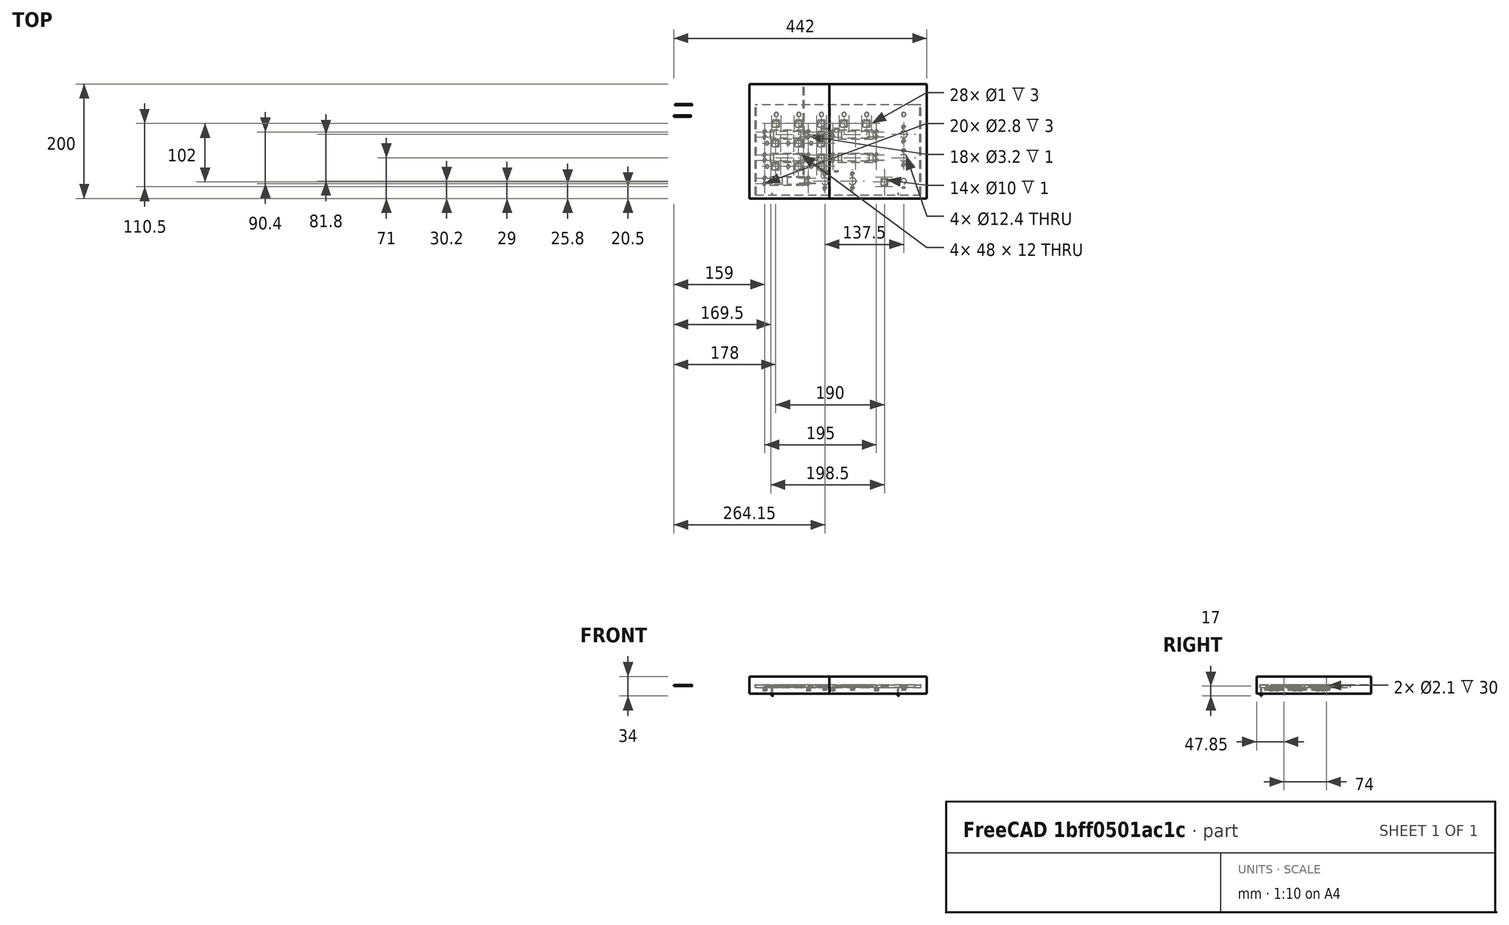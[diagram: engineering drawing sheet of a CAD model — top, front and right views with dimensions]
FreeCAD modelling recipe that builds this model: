
FCSTD DOCUMENT  (FreeCAD 0.17R13522 (Git))
Label: panel_frente_principal_con_spacers
License: CreativeCommons Attribution-ShareAlike
LicenseURL: http://creativecommons.org/licenses/by-sa/4.0/
objects: Part::Feature×53, Part::Cut×43, Part::Part2DObjectPython×22, Part::Fuse×22, Part::Box×13, Part::Cylinder×6, App::DocumentObjectGroup×3
note: 159 computed .brp shape members not serialized (recipe doc carries the construction recipe); baked Part::Feature solids carry a one-line shape summary decoded from their .brp

FEATURE [Part::Part2DObjectPython] Line009  # Draft 2D object (typed FeaturePython)
  ChamferSize = 0
  Closed = false
  End = (270.847,20.2,0)
  FilletRadius = 0
  Length = 35.3471
  MakeFace = false
  Points = (2) [(235.5,20.2,0),(270.847,20.2,0)]
  Start = (235.5,20.2,0)
  Subdivisions = 0
FEATURE [Part::Part2DObjectPython] Circle001  # Draft 2D object (typed FeaturePython)
  FirstAngle = 0
  LastAngle = 0
  MakeFace = false
  Placement = pos=(259.67,20.2,0) rot=(0,0,1;0rad)
  Radius = 14
FEATURE [Part::Part2DObjectPython] Line014  # Draft 2D object (typed FeaturePython)
  ChamferSize = 0
  Closed = false
  End = (248.272,28.2144,0)
  FilletRadius = 0
  Length = 13.696
  MakeFace = false
  Placement = pos=(-10,0,-4) rot=(0,0,1;0rad)
  Points = (2) [(269.378,20.2,4),(258.272,28.2144,4)]
  Start = (259.378,20.2,0)
  Subdivisions = 0
FEATURE [Part::Part2DObjectPython] Line015  # Draft 2D object (typed FeaturePython)
  ChamferSize = 0
  Closed = false
  End = (254.876,33.263,0)
  FilletRadius = 0
  Length = 13.7518
  MakeFace = false
  Placement = pos=(-10,0,-4) rot=(0,0,1;0rad)
  Points = (2) [(269.174,20.2,4),(264.876,33.263,4)]
  Start = (259.174,20.2,0)
  Subdivisions = 0
FEATURE [Part::Part2DObjectPython] Line016  # Draft 2D object (typed FeaturePython)
  ChamferSize = 0
  Closed = false
  End = (263.227,33.6931,0)
  FilletRadius = 0
  Length = 14.1488
  MakeFace = false
  Placement = pos=(-10,0,-4) rot=(0,0,1;0rad)
  Points = (2) [(268.97,20.2,4),(273.227,33.6931,4)]
  Start = (258.97,20.2,0)
  Subdivisions = 0
FEATURE [Part::Part2DObjectPython] Line017  # Draft 2D object (typed FeaturePython)
  ChamferSize = 0
  Closed = false
  End = (270.612,28.9289,0)
  FilletRadius = 0
  Length = 14.5511
  MakeFace = false
  Placement = pos=(-10,0,-4) rot=(0,0,1;0rad)
  Points = (2) [(268.97,20.2,4),(280.612,28.9289,4)]
  Start = (258.97,20.2,0)
  Subdivisions = 0
FEATURE [App::DocumentObjectGroup] Construction
  Group = -> [Line009,Circle001,Line014,Line015,Line016,Line017]
FEATURE [Part::Box] Box001  label="Cube"
  AttacherType = Attacher::AttachEngine3D
  Height = 3
  Length = 6
  Placement = pos=(39,81,-108) rot=(0,0,1;0rad)
  Width = 6
FEATURE [Part::Feature] Fusion008001001061001  label="panel_siplays_encoders_dobles_y_spacers"
  Placement = pos=(0,0,-105) rot=(0,0,1;0rad)
  shape: bbox 280 x 210 x 10 mm, 411 faces (baked)
FEATURE [Part::Feature] Fusion003002001  label="el perforador001"
  Placement = pos=(48,115,-108) rot=(0,1,0;3.14159rad)
  shape: bbox 22 x 12 x 18 mm, 19 faces (baked)
FEATURE [Part::Feature] Fusion003002001001  label="el perforador002"
  Placement = pos=(87.5,115,-108) rot=(0,1,0;3.14159rad)
  shape: bbox 22 x 12 x 18 mm, 19 faces (baked)
FEATURE [Part::Cut] Cut001001001002003001008002002004
  Base = -> Fusion008001001061001
  Refine = true
  Tool = -> Fusion003002001
FEATURE [Part::Feature] Fusion003002001001001  label="el perforador003"
  Placement = pos=(127,115,-108) rot=(0,1,0;3.14159rad)
  shape: bbox 22 x 12 x 18 mm, 19 faces (baked)
FEATURE [Part::Cut] Cut001001001002003001008002002005
  Base = -> Cut001001001002003001008002002004
  Refine = true
  Tool = -> Fusion003002001001
FEATURE [Part::Feature] Fusion003002001001001001  label="el perforador004"
  Placement = pos=(166.5,115,-108) rot=(0,1,0;3.14159rad)
  shape: bbox 22 x 12 x 18 mm, 19 faces (baked)
FEATURE [Part::Feature] Fusion003002001001001001001  label="el perforador005"
  Placement = pos=(206,115,-108) rot=(0,1,0;3.14159rad)
  shape: bbox 22 x 12 x 18 mm, 19 faces (baked)
FEATURE [Part::Cut] Cut001001001002003001008002002006
  Base = -> Cut001001001002003001008002002005
  Refine = true
  Tool = -> Fusion003002001001001001
FEATURE [Part::Cut] Cut001001001002003001008002002007
  Base = -> Cut001001001002003001008002002006
  Refine = true
  Tool = -> Fusion003002001001001001001
FEATURE [Part::Feature] Fusion003002001001001001002001001  label="el perforador008"
  Placement = pos=(127,40,-108) rot=(0,1,0;3.14159rad)
  shape: bbox 22 x 12 x 18 mm, 19 faces (baked)
FEATURE [Part::Feature] Fusion003002001001001001002001002  label="el perforador009"
  Placement = pos=(127,80.5,-108) rot=(0,1,0;3.14159rad)
  shape: bbox 22 x 12 x 18 mm, 19 faces (baked)
FEATURE [Part::Feature] Fusion003002001001001001002001  label="el perforador007"
  Placement = pos=(127,55,-108) rot=(0,1,0;3.14159rad)
  shape: bbox 22 x 12 x 18 mm, 19 faces (baked)
FEATURE [Part::Feature] Fusion003002001001001001002  label="el perforador006"
  Placement = pos=(127,95.5,-108) rot=(0,1,0;3.14159rad)
  shape: bbox 22 x 12 x 18 mm, 19 faces (baked)
FEATURE [Part::Cut] Cut001001001002003001008002002008
  Base = -> Cut001001001002003001008002002007
  Refine = true
  Tool = -> Fusion003002001001001
FEATURE [Part::Cut] Cut001001001002003001008002002009
  Base = -> Cut001001001002003001008002002008
  Refine = true
  Tool = -> Fusion003002001001001001002
FEATURE [Part::Cut] Cut001001001002003001008002002010
  Base = -> Cut001001001002003001008002002009
  Refine = true
  Tool = -> Fusion003002001001001001002001
FEATURE [Part::Box] Box001001002002002001003001001004001001001001001001002  label="Cube034"
  AttacherType = Attacher::AttachEngine3D
  Height = 4
  Length = 32
  Placement = pos=(200,15,-108) rot=(0,0,1;0rad)
  Width = 10
FEATURE [Part::Fuse] Fusion003002001001001001002001003
  Base = -> Cut001001001002003001008002002010
  Refine = true
  Tool = -> Box001001002002002001003001001004001001001001001001002
FEATURE [Part::Fuse] Fusion003002001001001001002001004
  Base = -> Box001001002002002001003001001004001001001001001001002
  Refine = true
  Tool = -> Fusion003002001001001001002001003
FEATURE [Part::Fuse] Fusion003002001001001001002001005
  Refine = true
  Tool = -> Fusion003002001001001001002001004
FEATURE [Part::Fuse] Fusion003002001001001001002001006
  Base = -> Box001
  Refine = true
  Tool = -> Fusion003002001001001001002001005
FEATURE [Part::Feature] Fusion003002001001001001002001002001  label="el perforador010"
  Placement = pos=(47,80.5,-108) rot=(0,1,0;3.14159rad)
  shape: bbox 22 x 12 x 18 mm, 19 faces (baked)
FEATURE [Part::Feature] Fusion003002001001001001002001002002  label="el perforador011"
  Placement = pos=(87,80.5,-108) rot=(0,1,0;3.14159rad)
  shape: bbox 22 x 12 x 18 mm, 19 faces (baked)
FEATURE [Part::Feature] Fusion003002001001001001002001001001  label="el perforador012"
  Placement = pos=(87,40,-108) rot=(0,1,0;3.14159rad)
  shape: bbox 22 x 12 x 18 mm, 19 faces (baked)
FEATURE [Part::Feature] Fusion003002001001001001002001001001001  label="el perforador013"
  Placement = pos=(47,40,-108) rot=(0,1,0;3.14159rad)
  shape: bbox 22 x 12 x 18 mm, 19 faces (baked)
FEATURE [Part::Cut] Cut001001001002003001008002002011
  Base = -> Fusion003002001001001001002001006
  Refine = true
  Tool = -> Fusion003002001001001001002001002
FEATURE [Part::Cut] Cut001001001002003001008002002012
  Base = -> Cut001001001002003001008002002011
  Refine = true
  Tool = -> Fusion003002001001001001002001002002
FEATURE [Part::Cut] Cut001001001002003001008002002013
  Base = -> Cut001001001002003001008002002012
  Refine = true
  Tool = -> Fusion003002001001001001002001002001
FEATURE [Part::Cut] Cut001001001002003001008002002014
  Base = -> Cut001001001002003001008002002013
  Refine = true
  Tool = -> Fusion003002001001001001002001001001001
FEATURE [Part::Feature] Fusion003002001001001001002001001001002  label="el perforador014"
  Placement = pos=(220,8,-108) rot=(0.707107,0.707107,0;3.14159rad)
  shape: bbox 12 x 22 x 18 mm, 19 faces (baked)
FEATURE [Part::Cut] Cut001001001002003001008002002015
  Base = -> Cut001001001002003001008002002014
  Refine = true
  Tool = -> Fusion003002001001001001002001001001
FEATURE [Part::Cut] Cut001001001002003001008002002016
  Base = -> Cut001001001002003001008002002015
  Refine = true
  Tool = -> Fusion003002001001001001002001001
FEATURE [Part::Cut] Cut001001001002003001008002002017  label="base solo faltan los leds"
  Base = -> Cut001001001002003001008002002016
  Refine = true
  Tool = -> Fusion003002001001001001002001001001002
FEATURE [Part::Feature] Fusion001001  label="perforador led 3 mm001 rojo com2"
  Placement = pos=(24,43,-108) rot=(0,1,0;3.14159rad)
  shape: bbox 6 x 6 x 10 mm, 13 faces (baked)
FEATURE [Part::Feature] Fusion003002001001001001002001001001003  label="perforador led 3 mm002 rojo nav2"
  Placement = pos=(61,43,-108) rot=(0,1,0;3.14159rad)
  shape: bbox 6 x 6 x 10 mm, 13 faces (baked)
FEATURE [Part::Feature] Fusion003002001001001001002001001001004  label="perforador led 3 mm002 rojo adf2"
  Placement = pos=(101,43,-108) rot=(0,1,0;3.14159rad)
  shape: bbox 6 x 6 x 10 mm, 13 faces (baked)
FEATURE [Part::Feature] Fusion003002001001001001002001001001005  label="perforador led 3 mm001 rojo com1"
  Placement = pos=(24,83.5,-108) rot=(0,1,0;3.14159rad)
  shape: bbox 6 x 6 x 10 mm, 13 faces (baked)
FEATURE [Part::Feature] Fusion003002001001001001002001001001006  label="perforador led 3 mm002 rojo nav1"
  Placement = pos=(61,83.5,-108) rot=(0,1,0;3.14159rad)
  shape: bbox 6 x 6 x 10 mm, 13 faces (baked)
FEATURE [Part::Feature] Fusion003002001001001001002001001001007  label="perforador led 3 mm002 rojo adf1"
  Placement = pos=(101,83.5,-108) rot=(0,1,0;3.14159rad)
  shape: bbox 6 x 6 x 10 mm, 13 faces (baked)
FEATURE [Part::Cut] Cut
  Base = -> Cut001001001002003001008002002017
  Refine = true
  Tool = -> Fusion003002001001001001002001001001005
FEATURE [Part::Cut] Cut001001001002003001008002002018
  Base = -> Cut
  Refine = true
  Tool = -> Fusion003002001001001001002001001001006
FEATURE [Part::Cut] Cut001001001002003001008002002019
  Base = -> Cut001001001002003001008002002018
  Refine = true
  Tool = -> Fusion003002001001001001002001001001007
FEATURE [Part::Cut] Cut001001001002003001008002002020
  Base = -> Cut001001001002003001008002002019
  Refine = true
  Tool = -> Fusion003002001001001001002001001001004
FEATURE [Part::Cut] Cut001001001002003001008002002021
  Base = -> Cut001001001002003001008002002020
  Refine = true
  Tool = -> Fusion003002001001001001002001001001003
FEATURE [Part::Cut] Cut001001001002003001008002002022
  Base = -> Cut001001001002003001008002002021
  Refine = true
  Tool = -> Fusion001001
FEATURE [Part::Feature] Fusion003002001001001001002001001001008  label="perforador led 5 mm sound marker"
  Placement = pos=(40.75,133,-108) rot=(0,1,0;3.14159rad)
  shape: bbox 7.5 x 7.5 x 10 mm, 13 faces (baked)
FEATURE [Part::Feature] Fusion003002001001001001002001001001009  label="perforador led 5 mm sound com1"
  Placement = pos=(80.25,133,-108) rot=(0,1,0;3.14159rad)
  shape: bbox 7.5 x 7.5 x 10 mm, 13 faces (baked)
FEATURE [Part::Feature] Fusion003002001001001001002001001001010  label="perforador led 5 mm sound nav1"
  Placement = pos=(119.75,133,-108) rot=(0,1,0;3.14159rad)
  shape: bbox 7.5 x 7.5 x 10 mm, 13 faces (baked)
FEATURE [Part::Feature] Fusion003002001001001001002001001001011  label="perforador led 5 mm sound dme"
  Placement = pos=(159.25,133,-108) rot=(0,1,0;3.14159rad)
  shape: bbox 7.5 x 7.5 x 10 mm, 13 faces (baked)
FEATURE [Part::Feature] Fusion003002001001001001002001001001012  label="perforador led 5 mm sound adf1"
  Placement = pos=(198.75,133,-108) rot=(0,1,0;3.14159rad)
  shape: bbox 7.5 x 7.5 x 10 mm, 13 faces (baked)
FEATURE [Part::Feature] Fusion003002001001001001002001001001013  label="perforador led 5 mm ON/OFF"
  Placement = pos=(263.5,133,-108) rot=(0,1,0;3.14159rad)
  shape: bbox 7.5 x 7.5 x 10 mm, 13 faces (baked)
FEATURE [Part::Cut] Cut001001001002003001008002002023
  Base = -> Cut001001001002003001008002002022
  Refine = true
  Tool = -> Fusion003002001001001001002001001001013
FEATURE [Part::Cut] Cut001001001002003001008002002024
  Base = -> Cut001001001002003001008002002023
  Refine = true
  Tool = -> Fusion003002001001001001002001001001012
FEATURE [Part::Cut] Cut001001001002003001008002002025
  Base = -> Cut001001001002003001008002002024
  Refine = true
  Tool = -> Fusion003002001001001001002001001001011
FEATURE [Part::Cut] Cut001001001002003001008002002026
  Base = -> Cut001001001002003001008002002025
  Refine = true
  Tool = -> Fusion003002001001001001002001001001010
FEATURE [Part::Cut] Cut001001001002003001008002002027
  Base = -> Cut001001001002003001008002002026
  Refine = true
  Tool = -> Fusion003002001001001001002001001001009
FEATURE [Part::Cut] Cut001001001002003001008002002028
  Base = -> Cut001001001002003001008002002027
  Refine = true
  Tool = -> Fusion003002001001001001002001001001008
FEATURE [Part::Box] Box  label="Cube035"
  AttacherType = Attacher::AttachEngine3D
  Height = 10
  Length = 300
  Placement = pos=(-8,153.85,-111) rot=(0,0,1;0rad)
  Width = 120
FEATURE [Part::Cut] Cut001001001002003001008002002029  label="panel sin letras"
  Base = -> Cut001001001002003001008002002028
  Refine = true
  Tool = -> Box
FEATURE [Part::Box] Box001001002002002001003001001004001001001001001001003  label="cortador saca parte izquierda"
  AttacherType = Attacher::AttachEngine3D
  Height = 30
  Length = 140
  Placement = pos=(-10,-10,-119) rot=(0,0,1;0rad)
  Width = 200
FEATURE [Part::Box] Box001001002002002001003001001004001001001001001001004  label="cortador saca parte derecha"
  AttacherType = Attacher::AttachEngine3D
  Height = 30
  Length = 170
  Placement = pos=(130,-10,-119) rot=(0,0,1;0rad)
  Width = 200
FEATURE [Part::Cylinder] Cylinder  label="clavija agujereadora1_1"
  Angle = 360
  AttacherType = Attacher::AttachEngine3D
  Height = 30
  Placement = pos=(115,111.85,-106) rot=(0,1,0;1.5708rad)
  Radius = 1.05
FEATURE [Part::Cylinder] Cylinder001  label="clavija agujereadora2_1"
  Angle = 360
  AttacherType = Attacher::AttachEngine3D
  Height = 30
  Placement = pos=(115,37.85,-106) rot=(0,1,0;1.5708rad)
  Radius = 1.05
FEATURE [Part::Cylinder] Cylinder002  label="clavija empalmadora1"
  Angle = 360
  AttacherType = Attacher::AttachEngine3D
  Height = 29.8
  Placement = pos=(-140,153.85,-105) rot=(0,1,0;1.5708rad)
  Radius = 1
FEATURE [Part::Cut] Cut001001001002003001008002002030
  Base = -> Cut001001001002003001008002002029
  Refine = true
  Tool = -> Cylinder
FEATURE [Part::Cut] Cut001001001002003001008002002031  label="panel sin letras con agujeros clavijas"
  Base = -> Cut001001001002003001008002002030
  Refine = true
  Tool = -> Cylinder001
FEATURE [App::DocumentObjectGroup] Group  label="cortadores principales"
  Group = -> [Box001001002002002001003001001004001001001001001001003,Box001001002002002001003001001004001001001001001001004]
FEATURE [Part::Cylinder] Cylinder003  label="clavija hace agujero"
  Angle = 360
  AttacherType = Attacher::AttachEngine3D
  Height = 30
  Placement = pos=(-142,133.85,-105) rot=(0,1,0;1.5708rad)
  Radius = 1.05
FEATURE [App::DocumentObjectGroup] Group001  label="clavijas"
  Group = -> [Cylinder003,Cylinder002]
FEATURE [Part::Box] Box001001002002002001003001001004001001001001001001006  label="fleje abajo"
  AttacherType = Attacher::AttachEngine3D
  Height = 4
  Length = 280
  Placement = pos=(0,-4,-108) rot=(0,0,1;0rad)
  Width = 4
FEATURE [Part::Fuse] Fusion
  Base = -> Cut001001001002003001008002002031
  Refine = true
  Tool = -> Box001001002002002001003001001004001001001001001001006
FEATURE [Part::Feature] Cylinder002001  label="clavija empalmadora une frente base"
  Placement = pos=(30,-2,-134) rot=(0,0,1;1.5708rad)
  shape: bbox 2 x 2 x 29.8 mm, 3 faces (baked)
FEATURE [Part::Feature] Cylinder002001001  label="clavija empalmadora une frente base2"
  Placement = pos=(250,-2,-134) rot=(0,0,1;1.5708rad)
  shape: bbox 2 x 2 x 29.8 mm, 3 faces (baked)
FEATURE [Part::Fuse] Fusion003002001001001001002001001001014
  Base = -> Fusion
  Refine = true
  Tool = -> Cylinder002001
FEATURE [Part::Fuse] Fusion003002001001001001002001001001015  label="frente con clavijas sin letras"
  Base = -> Cylinder002001001
  Refine = true
  Tool = -> Fusion003002001001001001002001001001014
FEATURE [Part::Box] Box001001002002002001003001001004001001001001001001007  label="cortador clavijas"
  AttacherType = Attacher::AttachEngine3D
  Height = 4
  Length = 280
  Placement = pos=(0,0,-153) rot=(1,0,0;1.5708rad)
  Width = 30
FEATURE [Part::Cut] Cut001001001002003001008002002032  label="frente con clavijas de 15 sin letras"
  Base = -> Fusion003002001001001001002001001001015
  Refine = true
  Tool = -> Box001001002002002001003001001004001001001001001001007
FEATURE [Part::Feature] Cut001001001002003001008002002033001001  label="circulo_para_botones002"
  Placement = pos=(29,39,-105) rot=(0,0,1;0rad)
  shape: bbox 14 x 14 x 1 mm, 7 faces (baked)
FEATURE [Part::Feature] Cut001001001002003001008002002033001001001  label="circulo_para_botones003"
  Placement = pos=(69,39,-105) rot=(0,0,1;0rad)
  shape: bbox 14 x 14 x 1 mm, 7 faces (baked)
FEATURE [Part::Feature] Cut001001001002003001008002002033001001001001  label="circulo_para_botones004"
  Placement = pos=(109,39,-105) rot=(0,0,1;0rad)
  shape: bbox 14 x 14 x 1 mm, 7 faces (baked)
FEATURE [Part::Feature] Cut001001001002003001008002002033001001001001001  label="circulo_para_botones005"
  Placement = pos=(109,54,-105) rot=(0,0,1;0rad)
  shape: bbox 14 x 14 x 1 mm, 7 faces (baked)
FEATURE [Part::Feature] Cut001001001002003001008002002033001001001001001001  label="circulo_para_botones006"
  Placement = pos=(109,79.5,-105) rot=(0,0,1;0rad)
  shape: bbox 14 x 14 x 1 mm, 7 faces (baked)
FEATURE [Part::Feature] Cut001001001002003001008002002033001001001001001001001  label="circulo_para_botones007"
  Placement = pos=(69,79.5,-105) rot=(0,0,1;0rad)
  shape: bbox 14 x 14 x 1 mm, 7 faces (baked)
FEATURE [Part::Feature] Cut001001001002003001008002002033001001001001001001001001  label="circulo_para_botones008"
  Placement = pos=(29,79.5,-105) rot=(0,0,1;0rad)
  shape: bbox 14 x 14 x 1 mm, 7 faces (baked)
FEATURE [Part::Feature] Cut001001001002003001008002002033001001001001001001001002  label="circulo_para_botones009"
  Placement = pos=(109,94.5,-105) rot=(0,0,1;0rad)
  shape: bbox 14 x 14 x 1 mm, 7 faces (baked)
FEATURE [Part::Feature] Cut001001001002003001008002002033001001001001001001001002001  label="circulo_para_botones010"
  Placement = pos=(109,114,-105) rot=(0,0,1;0rad)
  shape: bbox 14 x 14 x 1 mm, 7 faces (baked)
FEATURE [Part::Feature] Cut001001001002003001008002002033001001001001001001001002001001  label="circulo_para_botones011"
  Placement = pos=(69.5,114,-105) rot=(0,0,1;0rad)
  shape: bbox 14 x 14 x 1 mm, 7 faces (baked)
FEATURE [Part::Feature] Cut001001001002003001008002002033001001001001001001001002001001001  label="circulo_para_botones012"
  Placement = pos=(30,114,-105) rot=(0,0,1;0rad)
  shape: bbox 14 x 14 x 1 mm, 7 faces (baked)
FEATURE [Part::Feature] Cut001001001002003001008002002033001001001001001001001002001001002  label="circulo_para_botones013"
  Placement = pos=(148.5,114,-105) rot=(0,0,1;0rad)
  shape: bbox 14 x 14 x 1 mm, 7 faces (baked)
FEATURE [Part::Feature] Cut001001001002003001008002002033001001001001001001001002001001002001  label="circulo_para_botones014"
  Placement = pos=(188,114,-105) rot=(0,0,1;0rad)
  shape: bbox 14 x 14 x 1 mm, 7 faces (baked)
FEATURE [Part::Feature] Cut001001001002003001008002002033001001001001001001001002001001002001001  label="circulo_para_botones015"
  Placement = pos=(219,12,-105) rot=(0,0,1;0rad)
  shape: bbox 14 x 14 x 1 mm, 7 faces (baked)
FEATURE [Part::Fuse] Fusion003002001001001001002001001001016
  Base = -> Cut001001001002003001008002002032
  Refine = true
  Tool = -> Cut001001001002003001008002002033001001001001001001001002001001002001001
FEATURE [Part::Fuse] Fusion003002001001001001002001001001017
  Base = -> Cut001001001002003001008002002033001001001001001001001002001001002001
  Refine = true
  Tool = -> Fusion003002001001001001002001001001016
FEATURE [Part::Fuse] Fusion003002001001001001002001001001018
  Base = -> Cut001001001002003001008002002033001001001001001001001002001001002
  Refine = true
  Tool = -> Fusion003002001001001001002001001001017
FEATURE [Part::Fuse] Fusion003002001001001001002001001001019
  Base = -> Cut001001001002003001008002002033001001001001001001001002001001001
  Refine = true
  Tool = -> Fusion003002001001001001002001001001018
FEATURE [Part::Fuse] Fusion003002001001001001002001001001020
  Base = -> Cut001001001002003001008002002033001001001001001001001002001001
  Refine = true
  Tool = -> Fusion003002001001001001002001001001019
FEATURE [Part::Fuse] Fusion003002001001001001002001001001021
  Base = -> Cut001001001002003001008002002033001001001001001001001002001
  Refine = true
  Tool = -> Fusion003002001001001001002001001001020
FEATURE [Part::Fuse] Fusion003002001001001001002001001001022
  Base = -> Cut001001001002003001008002002033001001001001001001001002
  Refine = true
  Tool = -> Fusion003002001001001001002001001001021
FEATURE [Part::Fuse] Fusion003002001001001001002001001001023
  Base = -> Cut001001001002003001008002002033001001001001001001001001
  Refine = true
  Tool = -> Fusion003002001001001001002001001001022
FEATURE [Part::Fuse] Fusion003002001001001001002001001001024
  Base = -> Cut001001001002003001008002002033001001001001001001001
  Refine = true
  Tool = -> Fusion003002001001001001002001001001023
FEATURE [Part::Fuse] Fusion003002001001001001002001001001025
  Base = -> Cut001001001002003001008002002033001001001001001001
  Refine = true
  Tool = -> Fusion003002001001001001002001001001024
FEATURE [Part::Fuse] Fusion003002001001001001002001001001026
  Base = -> Cut001001001002003001008002002033001001001001001
  Refine = true
  Tool = -> Fusion003002001001001001002001001001025
FEATURE [Part::Fuse] Fusion003002001001001001002001001001027
  Base = -> Cut001001001002003001008002002033001001001001
  Refine = true
  Tool = -> Fusion003002001001001001002001001001026
FEATURE [Part::Fuse] Fusion003002001001001001002001001001028
  Base = -> Cut001001001002003001008002002033001001001
  Refine = true
  Tool = -> Fusion003002001001001001002001001001027
FEATURE [Part::Fuse] Fusion003002001001001001002001001001029  label="frente con botones redondeados falta leds recortar"
  Base = -> Cut001001001002003001008002002033001001
  Refine = true
  Tool = -> Fusion003002001001001001002001001001028
FEATURE [Part::Cylinder] Cylinder002001002  label="Cylinder"
  Angle = 360
  AttacherType = Attacher::AttachEngine3D
  Height = 40
  Placement = pos=(37,136.75,-132) rot=(0,0,1;0rad)
  Radius = 3.35
FEATURE [Part::Feature] Cylinder002001002001  label="Cylinder001"
  Placement = pos=(76.5,136.75,-132) rot=(0,0,1;0rad)
  shape: bbox 6.7 x 6.7 x 40 mm, 3 faces (baked)
FEATURE [Part::Feature] Cylinder002001002001001  label="Cylinder002"
  Placement = pos=(116,136.75,-132) rot=(0,0,1;0rad)
  shape: bbox 6.7 x 6.7 x 40 mm, 3 faces (baked)
FEATURE [Part::Feature] Cylinder002001002001001001  label="Cylinder003"
  Placement = pos=(155.5,136.75,-132) rot=(0,0,1;0rad)
  shape: bbox 6.7 x 6.7 x 40 mm, 3 faces (baked)
FEATURE [Part::Feature] Cylinder002001002001001001001  label="Cylinder004"
  Placement = pos=(195,136.75,-132) rot=(0,0,1;0rad)
  shape: bbox 6.7 x 6.7 x 40 mm, 3 faces (baked)
FEATURE [Part::Feature] Cylinder002001002001001001001001  label="Cylinder005"
  Placement = pos=(260,136.75,-132) rot=(0,0,1;0rad)
  shape: bbox 6.7 x 6.7 x 40 mm, 3 faces (baked)
FEATURE [Part::Cut] Cut001001001002003001008002002033001001001001001001001002001001002001002
  Base = -> Fusion003002001001001001002001001001029
  Refine = true
  Tool = -> Cylinder002001002
FEATURE [Part::Cut] Cut001001001002003001008002002033001001001001001001001002001001002001003
  Base = -> Cut001001001002003001008002002033001001001001001001001002001001002001002
  Refine = true
  Tool = -> Cylinder002001002001
FEATURE [Part::Cut] Cut001001001002003001008002002033001001001001001001001002001001002001004
  Base = -> Cut001001001002003001008002002033001001001001001001001002001001002001003
  Refine = true
  Tool = -> Cylinder002001002001001
FEATURE [Part::Cut] Cut001001001002003001008002002033001001001001001001001002001001002001005
  Base = -> Cut001001001002003001008002002033001001001001001001001002001001002001004
  Refine = true
  Tool = -> Cylinder002001002001001001
FEATURE [Part::Cut] Cut001001001002003001008002002033001001001001001001001002001001002001006
  Base = -> Cut001001001002003001008002002033001001001001001001001002001001002001005
  Refine = true
  Tool = -> Cylinder002001002001001001001
FEATURE [Part::Cut] Cut001001001002003001008002002033001001001001001001001002001001002001007
  Base = -> Cut001001001002003001008002002033001001001001001001001002001001002001006
  Refine = true
  Tool = -> Cylinder002001002001001001001001
FEATURE [Part::Cylinder] Cylinder002001002001001001001002  label="Cylinder006"
  Angle = 360
  AttacherType = Attacher::AttachEngine3D
  Height = 60
  Placement = pos=(21,46,-142.75) rot=(0,0,1;0rad)
  Radius = 2.65
FEATURE [Part::Feature] Cylinder002001002001001001001002001  label="Cylinder007"
  Placement = pos=(58,46,-141.75) rot=(0,0,1;0rad)
  shape: bbox 5.3 x 5.3 x 60 mm, 3 faces (baked)
FEATURE [Part::Feature] Cylinder002001002001001001001002001001  label="Cylinder008"
  Placement = pos=(98,46,-141.75) rot=(0,0,1;0rad)
  shape: bbox 5.3 x 5.3 x 60 mm, 3 faces (baked)
FEATURE [Part::Feature] Cylinder002001002001001001001002001001001  label="Cylinder009"
  Placement = pos=(98,86.5,-141.75) rot=(0,0,1;0rad)
  shape: bbox 5.3 x 5.3 x 60 mm, 3 faces (baked)
FEATURE [Part::Feature] Cylinder002001002001001001001002001001001001  label="Cylinder010"
  Placement = pos=(58,86.5,-141.75) rot=(0,0,1;0rad)
  shape: bbox 5.3 x 5.3 x 60 mm, 3 faces (baked)
FEATURE [Part::Feature] Cylinder002001002001001001001002001001001001001  label="Cylinder011"
  Placement = pos=(21,86.5,-141.75) rot=(0,0,1;0rad)
  shape: bbox 5.3 x 5.3 x 60 mm, 3 faces (baked)
FEATURE [Part::Cut] Cut001001001002003001008002002033001001001001001001001002001001002001008
  Base = -> Cut001001001002003001008002002033001001001001001001001002001001002001007
  Refine = true
  Tool = -> Cylinder002001002001001001001002
FEATURE [Part::Cut] Cut001001001002003001008002002033001001001001001001001002001001002001009
  Base = -> Cut001001001002003001008002002033001001001001001001001002001001002001008
  Refine = true
  Tool = -> Cylinder002001002001001001001002001
FEATURE [Part::Cut] Cut001001001002003001008002002033001001001001001001001002001001002001010
  Base = -> Cut001001001002003001008002002033001001001001001001001002001001002001009
  Refine = true
  Tool = -> Cylinder002001002001001001001002001001
FEATURE [Part::Cut] Cut001001001002003001008002002033001001001001001001001002001001002001011
  Base = -> Cut001001001002003001008002002033001001001001001001001002001001002001010
  Refine = true
  Tool = -> Cylinder002001002001001001001002001001001001001
FEATURE [Part::Cut] Cut001001001002003001008002002033001001001001001001001002001001002001012
  Base = -> Cut001001001002003001008002002033001001001001001001001002001001002001011
  Refine = true
  Tool = -> Cylinder002001002001001001001002001001001001
FEATURE [Part::Cut] Cut001001001002003001008002002033001001001001001001001002001001002001013  label="panel frente sin letras"
  Base = -> Cut001001001002003001008002002033001001001001001001001002001001002001012
  Refine = true
  Tool = -> Cylinder002001002001001001001002001001001
FEATURE [Part::Box] Box001001002002002001003001001004001001001001001001008  label="Cube036"
  AttacherType = Attacher::AttachEngine3D
  Height = 50
  Length = 4
  Placement = pos=(257.6,7.5,-116) rot=(0,0,1;0rad)
  Width = 2.5
FEATURE [Part::Cut] Cut001001001002003001008002002033001001001001001001001002001001002001014  label="panel frente sin letras todos los agujeros"
  Base = -> Cut001001001002003001008002002033001001001001001001001002001001002001013
  Refine = true
  Tool = -> Box001001002002002001003001001004001001001001001001008
FEATURE [Part::Part2DObjectPython] ShapeString  label="texto marker"  # Draft 2D object (typed FeaturePython)
  FontFile = <userpath>/Desktop/cad/Arimo/Arimo-Bold.ttf
  Placement = pos=(4.94,131.3,-104) rot=(0,0,1;0rad)
  Size = 6
  String = Marker
  Support = -> [Cut001001001002003001008002002033001001001001001001001002001001002001014]
  Tracking = 0
FEATURE [Part::Part2DObjectPython] ShapeString001  label="texto com1"  # Draft 2D object (typed FeaturePython)
  FontFile = <userpath>/Desktop/cad/Arimo/Arimo-Bold.ttf
  Placement = pos=(45.56,131.3,-104) rot=(0,0,1;0rad)
  Size = 6
  String = COM-1
  Support = -> [Cut001001001002003001008002002033001001001001001001001002001001002001014]
  Tracking = 0
FEATURE [Part::Part2DObjectPython] ShapeString002  label="texto nav1"  # Draft 2D object (typed FeaturePython)
  FontFile = <userpath>/Desktop/cad/Arimo/Arimo-Bold.ttf
  Placement = pos=(88.83,131.3,-104) rot=(0,0,1;0rad)
  Size = 6
  String = NAV-1
  Support = -> [Cut001001001002003001008002002033001001001001001001001002001001002001014]
  Tracking = 0
FEATURE [Part::Part2DObjectPython] ShapeString003  label="texto dme"  # Draft 2D object (typed FeaturePython)
  FontFile = <userpath>/Desktop/cad/Arimo/Arimo-Bold.ttf
  Placement = pos=(132.68,131.3,-104) rot=(0,0,1;0rad)
  Size = 6
  String = DME
  Support = -> [Cut001001001002003001008002002033001001001001001001001002001001002001014]
  Tracking = 0
FEATURE [Part::Part2DObjectPython] ShapeString004  label="texto adf1"  # Draft 2D object (typed FeaturePython)
  FontFile = <userpath>/Desktop/cad/Arimo/Arimo-Bold.ttf
  Placement = pos=(167.99,131.3,-104) rot=(0,0,1;0rad)
  Size = 6
  String = ADF-1
  Support = -> [Cut001001001002003001008002002033001001001001001001001002001001002001014]
  Tracking = 0
FEATURE [Part::Part2DObjectPython] ShapeString005  label="texto On"  # Draft 2D object (typed FeaturePython)
  FontFile = <userpath>/Desktop/cad/Arimo/Arimo-Bold.ttf
  Placement = pos=(243.54,134.27,-104) rot=(0,0,1;0rad)
  Size = 6
  String = On
  Support = -> [Cut001001001002003001008002002033001001001001001001001002001001002001014]
  Tracking = 0
FEATURE [Part::Part2DObjectPython] ShapeString006  label="texto sel com1"  # Draft 2D object (typed FeaturePython)
  FontFile = <userpath>/Desktop/cad/Arimo/Arimo-Bold.ttf
  Placement = pos=(17.6,72.3,-104) rot=(0,0,1;0rad)
  Size = 6
  String = COM-1
  Support = -> [Cut001001001002003001008002002033001001001001001001001002001001002001014]
  Tracking = 0
FEATURE [Part::Part2DObjectPython] ShapeString007  label="texto sel nav1"  # Draft 2D object (typed FeaturePython)
  FontFile = <userpath>/Desktop/cad/Arimo/Arimo-Bold.ttf
  Placement = pos=(56.95,72.3,-104) rot=(0,0,1;0rad)
  Size = 6
  String = NAV-1
  Support = -> [Cut001001001002003001008002002033001001001001001001001002001001002001014]
  Tracking = 0
FEATURE [Part::Part2DObjectPython] ShapeString008  label="texto sel adf1"  # Draft 2D object (typed FeaturePython)
  FontFile = <userpath>/Desktop/cad/Arimo/Arimo-Bold.ttf
  Placement = pos=(98.13,72.3,-104) rot=(0,0,1;0rad)
  Size = 6
  String = ADF-1
  Tracking = 0
FEATURE [Part::Part2DObjectPython] ShapeString009  label="texto sel com2"  # Draft 2D object (typed FeaturePython)
  FontFile = <userpath>/Desktop/cad/Arimo/Arimo-Bold.ttf
  Placement = pos=(17.6,32.4,-104) rot=(0,0,1;0rad)
  Size = 6
  String = COM-2
  Tracking = 0
FEATURE [Part::Part2DObjectPython] ShapeString010  label="texto sel nav2"  # Draft 2D object (typed FeaturePython)
  FontFile = <userpath>/Desktop/cad/Arimo/Arimo-Bold.ttf
  Placement = pos=(56.95,32.4,-104) rot=(0,0,1;0rad)
  Size = 6
  String = NAV-2
  Support = -> [Cut001001001002003001008002002033001001001001001001001002001001002001014]
  Tracking = 0
FEATURE [Part::Part2DObjectPython] ShapeString011  label="texto sel adf2"  # Draft 2D object (typed FeaturePython)
  FontFile = <userpath>/Desktop/cad/Arimo/Arimo-Bold.ttf
  Placement = pos=(98.13,32.4,-104) rot=(0,0,1;0rad)
  Size = 6
  String = ADF-2
  Tracking = 0
FEATURE [Part::Part2DObjectPython] ShapeString012  label="texto transponder"  # Draft 2D object (typed FeaturePython)
  FontFile = <userpath>/Desktop/cad/Arimo/Arimo-Bold.ttf
  Placement = pos=(35.92,5,-104) rot=(0,0,1;0rad)
  Size = 6
  String = Transponder
  Tracking = 0
FEATURE [Part::Part2DObjectPython] ShapeString013  label="texto ident"  # Draft 2D object (typed FeaturePython)
  FontFile = <userpath>/Desktop/cad/Arimo/Arimo-Bold.ttf
  Placement = pos=(217.09,5,-104) rot=(0,0,1;0rad)
  Size = 6
  String = Ident
  Support = -> [Cut001001001002003001008002002033001001001001001001001002001001002001014]
  Tracking = 0
FEATURE [Part::Part2DObjectPython] ShapeString014  label="texto test"  # Draft 2D object (typed FeaturePython)
  FontFile = <userpath>/Desktop/cad/Arimo/Arimo-Bold.ttf
  Placement = pos=(233.76,20,-104) rot=(0,0,1;0rad)
  Size = 5
  String = test
  Tracking = 0
FEATURE [Part::Part2DObjectPython] ShapeString015  label="texto Gnd"  # Draft 2D object (typed FeaturePython)
  FontFile = <userpath>/Desktop/cad/Arimo/Arimo-Bold.ttf
  Placement = pos=(272.614,20.1887,-104) rot=(0,0,1;0rad)
  Size = 5
  String = Gnd
  Support = -> [Cut001001001002003001008002002033001001001001001001001002001001002001014]
  Tracking = 0
FEATURE [Part::Box] Box001001002002002001003001001004001001001001001001009  label="Cube037"
  AttacherType = Attacher::AttachEngine3D
  Height = 4
  Length = 10
  Placement = pos=(280,-4,-108) rot=(0,0,1;0rad)
  Width = 158
FEATURE [Part::Fuse] Fusion003002001001001001002001001001030
  Base = -> Cut001001001002003001008002002033001001001001001001001002001001002001014
  Refine = true
  Tool = -> Box001001002002002001003001001004001001001001001001009
FEATURE [Part::Box] Box001001002002002001003001001004001001001001001001010  label="Cube038"
  AttacherType = Attacher::AttachEngine3D
  Height = 0.5
  Length = 2
  Placement = pos=(129.5,-4,-104) rot=(0,0,1;0rad)
  Width = 157.85
FEATURE [Part::Box] Box001001002002002001003001001004001001001001001001011  label="Cube039"
  AttacherType = Attacher::AttachEngine3D
  Height = 0.5
  Length = 2
  Placement = pos=(84,32,-104) rot=(0,0,1;0rad)
  Width = 157.85
FEATURE [Part::Box] Box001001002002002001003001001004001001001001001001012  label="Cube040"
  AttacherType = Attacher::AttachEngine3D
  Height = 0.5
  Length = 2
  Placement = pos=(0,-4,-104) rot=(0,0,1;0rad)
  Width = 157.85
FEATURE [Part::Box] Box001001002002002001003001001004001001001001001001013  label="Cube041"
  AttacherType = Attacher::AttachEngine3D
  Height = 0.5
  Length = 2
  Placement = pos=(288,-4,-104) rot=(0,0,1;0rad)
  Width = 157.85
